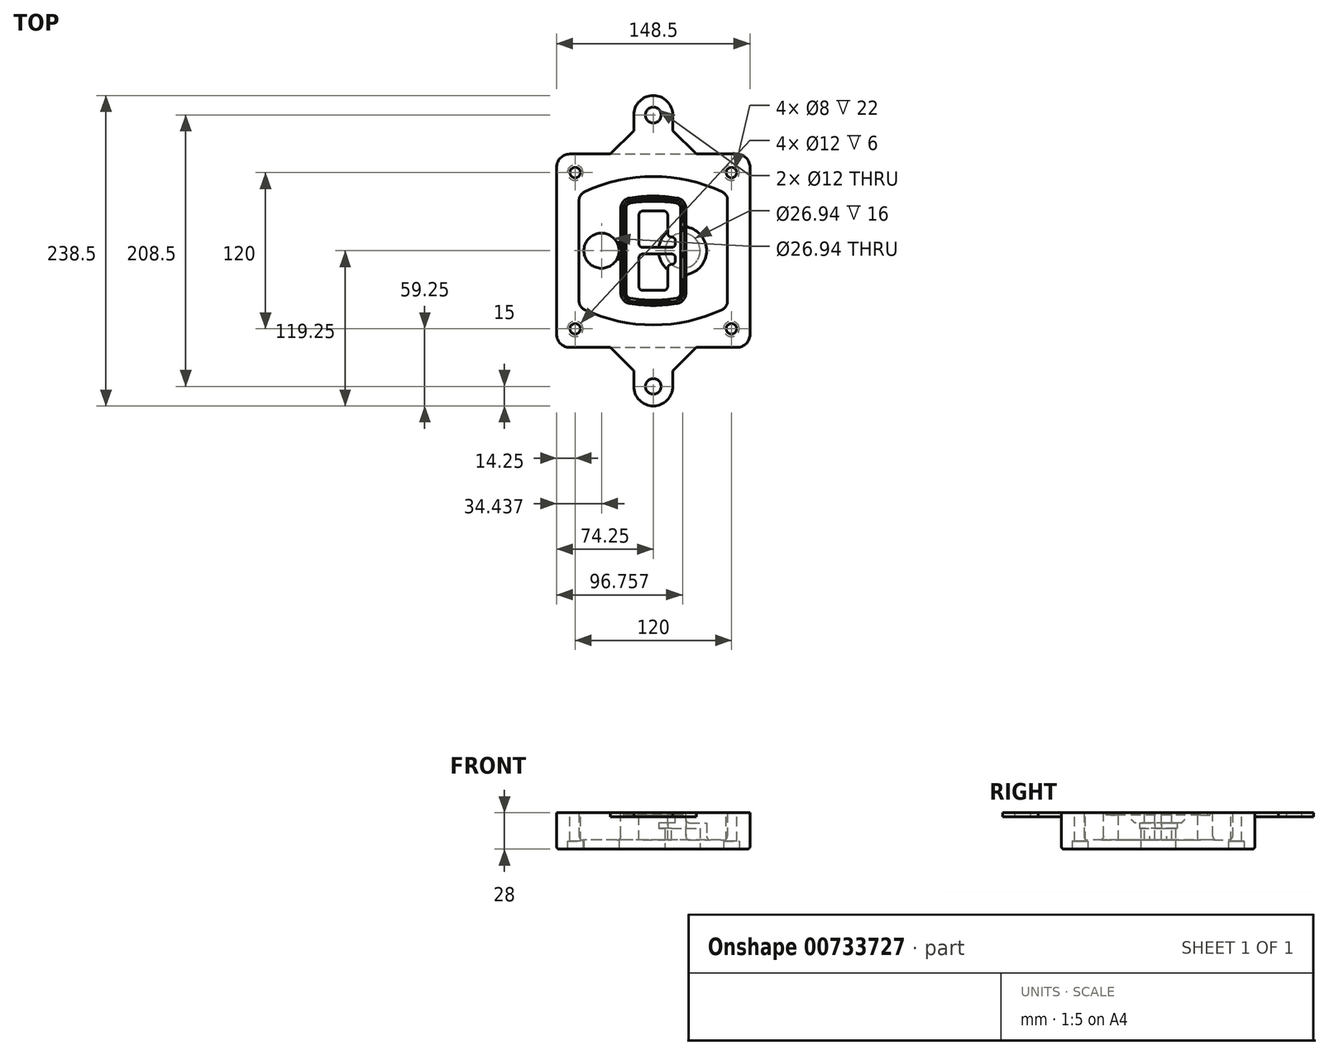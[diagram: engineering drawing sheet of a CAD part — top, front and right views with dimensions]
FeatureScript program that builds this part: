
annotation { "Feature Type Name" : "Feature", "Feature Type Description" : "" }
export const myFeature = defineFeature(function(context is Context, id is Id, definition is map)
    precondition{}
    {
        {
            var Q0;
            Q0=qCreatedBy(makeId("Top.planeOp"),FACE);
            var sketch = newSketch(context, id + "F0", { "sketchPlane" : qUnion([Q0])});
            skPoint(sketch, "E0.rect.middle", {"position": v(0, 0) * mm});
            skLineSegment(sketch, "E1.bottom", {"start": v(-64.25, -74.25) * mm, "end": v(64.25, -74.25) * mm});
            skLineSegment(sketch, "E1.top", {"start": v(-64.25, 74.25) * mm, "end": v(64.25, 74.25) * mm});
            skLineSegment(sketch, "E1.left", {"start": v(-74.25, -64.25) * mm, "end": v(-74.25, 64.25) * mm});
            skLineSegment(sketch, "E1.right", {"start": v(74.25, -64.25) * mm, "end": v(74.25, 64.25) * mm});
            skLineSegment(sketch, "E2", {"start": v(-74.25, 74.25) * mm, "end": v(74.25, -74.25) * mm, "construction": true});
            skLineSegment(sketch, "E3", {"start": v(74.25, 74.25) * mm, "end": v(-74.25, -74.25) * mm, "construction": true});
            skCircle(sketch, "E4", {"center": v(-60, 60) * mm, "radius": 4 * mm});
            skCircle(sketch, "E5", {"center": v(60, 60) * mm, "radius": 4 * mm});
            skCircle(sketch, "E6", {"center": v(60, -60) * mm, "radius": 4 * mm});
            skCircle(sketch, "E7", {"center": v(-60, -60) * mm, "radius": 4 * mm});
            skLineSegment(sketch, "E8", {"start": v(-60, 60) * mm, "end": v(60, 60) * mm, "construction": true});
            skLineSegment(sketch, "E9", {"start": v(60, 60) * mm, "end": v(60, -60) * mm, "construction": true});
            skLineSegment(sketch, "E10", {"start": v(60, -60) * mm, "end": v(-60, -60) * mm, "construction": true});
            skLineSegment(sketch, "E11", {"start": v(-60, -60) * mm, "end": v(-60, 60) * mm, "construction": true});
            skLineSegment(sketch, "E12", {"start": v(-60, 38.83) * mm, "end": v(-60, -38.83) * mm});
            skLineSegment(sketch, "E13", {"start": v(60, 38.83) * mm, "end": v(60, -38.83) * mm});
            skArc(sketch, "E14", {"start": v(54.26, 47.88) * mm, "mid": v(0, 60) * mm, "end": v(-54.26, 47.88) * mm});
            skArc(sketch, "E15", {"start": v(-54.26, -47.88) * mm, "mid": v(0, -60) * mm, "end": v(54.26, -47.88) * mm});
            skLineSegment(sketch, "E16", {"start": v(-60, 0) * mm, "end": v(60, 0) * mm, "construction": true});
            skPoint(sketch, "E17.visualSharp", {"position": v(-60, -45) * mm});
            skArc(sketch, "E17.filletArc", {"start": v(-60, -38.83) * mm, "mid": v(-58.44, -44.2) * mm, "end": v(-54.26, -47.88) * mm});
            skPoint(sketch, "E18.visualSharp", {"position": v(-60, 45) * mm});
            skArc(sketch, "E18.filletArc", {"start": v(-54.26, 47.88) * mm, "mid": v(-58.44, 44.2) * mm, "end": v(-60, 38.83) * mm});
            skPoint(sketch, "E19.visualSharp", {"position": v(60, 45) * mm});
            skArc(sketch, "E19.filletArc", {"start": v(60, 38.83) * mm, "mid": v(58.44, 44.2) * mm, "end": v(54.26, 47.88) * mm});
            skPoint(sketch, "E20.visualSharp", {"position": v(60, -45) * mm});
            skArc(sketch, "E20.filletArc", {"start": v(54.26, -47.88) * mm, "mid": v(58.44, -44.2) * mm, "end": v(60, -38.83) * mm});
            skPoint(sketch, "E21.visualSharp", {"position": v(-74.25, 74.25) * mm});
            skArc(sketch, "E21.filletArc", {"start": v(-64.25, 74.25) * mm, "mid": v(-71.32, 71.32) * mm, "end": v(-74.25, 64.25) * mm});
            skPoint(sketch, "E22.visualSharp", {"position": v(74.25, 74.25) * mm});
            skArc(sketch, "E22.filletArc", {"start": v(74.25, 64.25) * mm, "mid": v(71.32, 71.32) * mm, "end": v(64.25, 74.25) * mm});
            skPoint(sketch, "E23.visualSharp", {"position": v(74.25, -74.25) * mm});
            skArc(sketch, "E23.filletArc", {"start": v(64.25, -74.25) * mm, "mid": v(71.32, -71.32) * mm, "end": v(74.25, -64.25) * mm});
            skPoint(sketch, "E24.visualSharp", {"position": v(-74.25, -74.25) * mm});
            skArc(sketch, "E24.filletArc", {"start": v(-74.25, -64.25) * mm, "mid": v(-71.32, -71.32) * mm, "end": v(-64.25, -74.25) * mm});
            skArc(sketch, "E25.0", {"start": v(57, 38.83) * mm, "mid": v(55.9, 42.58) * mm, "end": v(52.98, 45.17) * mm});
            skLineSegment(sketch, "E25.1", {"start": v(57, 38.83) * mm, "end": v(57, -38.83) * mm});
            skArc(sketch, "E25.2", {"start": v(52.98, -45.17) * mm, "mid": v(55.9, -42.58) * mm, "end": v(57, -38.83) * mm});
            skArc(sketch, "E25.3", {"start": v(-52.98, -45.17) * mm, "mid": v(0, -57) * mm, "end": v(52.98, -45.17) * mm});
            skArc(sketch, "E25.4", {"start": v(-57, -38.83) * mm, "mid": v(-55.9, -42.58) * mm, "end": v(-52.98, -45.17) * mm});
            skArc(sketch, "E25.5", {"start": v(52.98, 45.17) * mm, "mid": v(0, 57) * mm, "end": v(-52.98, 45.17) * mm});
            skLineSegment(sketch, "E25.6", {"start": v(-57, 38.83) * mm, "end": v(-57, -38.83) * mm});
            skArc(sketch, "E25.7", {"start": v(-52.98, 45.17) * mm, "mid": v(-55.9, 42.58) * mm, "end": v(-57, 38.83) * mm});
            skArc(sketch, "E26.0", {"start": v(-55.96, 51.5) * mm, "mid": v(-61.82, 46.33) * mm, "end": v(-64, 38.83) * mm});
            skArc(sketch, "E26.1", {"start": v(55.96, 51.5) * mm, "mid": v(0, 64) * mm, "end": v(-55.96, 51.5) * mm});
            skArc(sketch, "E26.2", {"start": v(64, 38.83) * mm, "mid": v(61.82, 46.33) * mm, "end": v(55.96, 51.5) * mm});
            skLineSegment(sketch, "E26.3", {"start": v(64, 38.83) * mm, "end": v(64, -38.83) * mm});
            skArc(sketch, "E26.4", {"start": v(55.96, -51.5) * mm, "mid": v(61.82, -46.33) * mm, "end": v(64, -38.83) * mm});
            skLineSegment(sketch, "E26.5", {"start": v(-64, 38.83) * mm, "end": v(-64, -38.83) * mm});
            skArc(sketch, "E26.6", {"start": v(-55.96, -51.5) * mm, "mid": v(0, -64) * mm, "end": v(55.96, -51.5) * mm});
            skArc(sketch, "E26.7", {"start": v(-64, -38.83) * mm, "mid": v(-61.82, -46.33) * mm, "end": v(-55.96, -51.5) * mm});
            skSolve(sketch);
        }
        {
            var Q0;
            Q0=makeQuery(id+"F0.imprint","IMPRINT",FACE,{"disambiguationData":[TD([[makeQuery(id+"F0.imprint","IMPRINT",EDGE,{"derivedFrom":sQuery(id+"F0.wireOp",EDGE,"E1.bottom")}),1.0]])]});
            var Q1;
            Q1=makeQuery(id+"F0.imprint","IMPRINT",FACE,{"disambiguationData":[TD([[makeQuery(id+"F0.imprint","IMPRINT",EDGE,{"derivedFrom":sQuery(id+"F0.wireOp",EDGE,"E12")}),1.0]])]});
            var Q2;
            Q2=makeQuery(id+"F0.imprint","IMPRINT",FACE,{"disambiguationData":[TD([[makeQuery(id+"F0.imprint","IMPRINT",EDGE,{"derivedFrom":sQuery(id+"F0.wireOp",EDGE,"E25.0")}),1.0]])]});
            var Q3;
            Q3=makeQuery(id+"F0.imprint","IMPRINT",FACE,{"disambiguationData":[TD([[makeQuery(id+"F0.imprint","IMPRINT",EDGE,{"derivedFrom":sQuery(id+"F0.wireOp",EDGE,"E12")}),-1.0]])]});
            extrude(context, id + "F1", {"entities" : qUnion([Q0, Q1, Q2, Q3]), "oppositeDirection" : true, "depth" : 25 * mm});
        }
        {
            var Q0;
            Q0=makeQuery(id+"F0.imprint","IMPRINT",FACE,{"disambiguationData":[TD([[makeQuery(id+"F0.imprint","IMPRINT",EDGE,{"derivedFrom":sQuery(id+"F0.wireOp",EDGE,"E12")}),1.0]])]});
            extrude(context, id + "F2", {"entities" : qUnion([Q0]), "operationType" : NewBodyOperationType.ADD, "depth" : 3 * mm});
        }
        {
            var Q0;
            Q0=makeQuery(id+"F0.imprint","IMPRINT",FACE,{"disambiguationData":[TD([[makeQuery(id+"F0.imprint","IMPRINT",EDGE,{"derivedFrom":sQuery(id+"F0.wireOp",EDGE,"E25.0")}),1.0]])]});
            extrude(context, id + "F3", {"entities" : qUnion([Q0]), "operationType" : NewBodyOperationType.REMOVE, "oppositeDirection" : true, "depth" : 18 * mm});
        }
        {
            var Q0;
            Q0=makeQuery(id+"F2.opExtrude","CAP_FACE",FACE,{"disambiguationData":[OSD([sQuery(id+"F0.wireOp",EDGE,"E12"),sQuery(id+"F0.wireOp",EDGE,"E13"),sQuery(id+"F0.wireOp",EDGE,"E14"),sQuery(id+"F0.wireOp",EDGE,"E15"),sQuery(id+"F0.wireOp",EDGE,"E17.filletArc"),sQuery(id+"F0.wireOp",EDGE,"E18.filletArc"),sQuery(id+"F0.wireOp",EDGE,"E19.filletArc"),sQuery(id+"F0.wireOp",EDGE,"E20.filletArc"),sQuery(id+"F0.wireOp",EDGE,"E25.0"),sQuery(id+"F0.wireOp",EDGE,"E25.1"),sQuery(id+"F0.wireOp",EDGE,"E25.2"),sQuery(id+"F0.wireOp",EDGE,"E25.3"),sQuery(id+"F0.wireOp",EDGE,"E25.4"),sQuery(id+"F0.wireOp",EDGE,"E25.5"),sQuery(id+"F0.wireOp",EDGE,"E25.6"),sQuery(id+"F0.wireOp",EDGE,"E25.7")])],"isStart":false});
            var sketch = newSketch(context, id + "F4", { "sketchPlane" : qUnion([Q0])});
            skArc(sketch, "E27.0", {"start": v(-18.34, -40.45) * mm, "mid": v(0, -42) * mm, "end": v(18.34, -40.45) * mm});
            skArc(sketch, "E28.0", {"start": v(18.34, 40.45) * mm, "mid": v(0, 42) * mm, "end": v(-18.34, 40.45) * mm});
            skLineSegment(sketch, "E29", {"start": v(-25, 32.57) * mm, "end": v(-25, -32.57) * mm});
            skLineSegment(sketch, "E30", {"start": v(25, 32.57) * mm, "end": v(25, -32.57) * mm});
            skLineSegment(sketch, "E31", {"start": v(-25, 39.1) * mm, "end": v(25, 39.1) * mm, "construction": true});
            skLineSegment(sketch, "E32", {"start": v(-25, -39.1) * mm, "end": v(25, -39.1) * mm, "construction": true});
            skPoint(sketch, "E33.visualSharp", {"position": v(-25, 39.1) * mm});
            skArc(sketch, "E33.filletArc", {"start": v(-18.34, 40.45) * mm, "mid": v(-23.11, 37.73) * mm, "end": v(-25, 32.57) * mm});
            skPoint(sketch, "E34.visualSharp", {"position": v(25, 39.1) * mm});
            skArc(sketch, "E34.filletArc", {"start": v(25, 32.57) * mm, "mid": v(23.11, 37.73) * mm, "end": v(18.34, 40.45) * mm});
            skPoint(sketch, "E35.visualSharp", {"position": v(25, -39.1) * mm});
            skArc(sketch, "E35.filletArc", {"start": v(18.34, -40.45) * mm, "mid": v(23.11, -37.73) * mm, "end": v(25, -32.57) * mm});
            skPoint(sketch, "E36.visualSharp", {"position": v(-25, -39.1) * mm});
            skArc(sketch, "E36.filletArc", {"start": v(-25, -32.57) * mm, "mid": v(-23.11, -37.73) * mm, "end": v(-18.34, -40.45) * mm});
            skArc(sketch, "E37.0", {"start": v(52.98, 45.17) * mm, "mid": v(0, 57) * mm, "end": v(-52.98, 45.17) * mm});
            skArc(sketch, "E37.1", {"start": v(-52.98, 45.17) * mm, "mid": v(-55.9, 42.58) * mm, "end": v(-57, 38.83) * mm});
            skLineSegment(sketch, "E37.2", {"start": v(-57, 38.83) * mm, "end": v(-57, -38.83) * mm});
            skArc(sketch, "E37.3", {"start": v(-57, -38.83) * mm, "mid": v(-55.9, -42.58) * mm, "end": v(-52.98, -45.17) * mm});
            skArc(sketch, "E37.4", {"start": v(-52.98, -45.17) * mm, "mid": v(0, -57) * mm, "end": v(52.98, -45.17) * mm});
            skArc(sketch, "E37.5", {"start": v(52.98, -45.17) * mm, "mid": v(55.9, -42.58) * mm, "end": v(57, -38.83) * mm});
            skLineSegment(sketch, "E37.6", {"start": v(57, 38.83) * mm, "end": v(57, -38.83) * mm});
            skArc(sketch, "E37.7", {"start": v(57, 38.83) * mm, "mid": v(55.9, 42.58) * mm, "end": v(52.98, 45.17) * mm});
            skLineSegment(sketch, "E38.0", {"start": v(23, 32.57) * mm, "end": v(23, -32.57) * mm});
            skArc(sketch, "E38.1", {"start": v(18, -38.48) * mm, "mid": v(21.58, -36.44) * mm, "end": v(23, -32.57) * mm});
            skArc(sketch, "E38.2", {"start": v(-18, -38.48) * mm, "mid": v(0, -40) * mm, "end": v(18, -38.48) * mm});
            skArc(sketch, "E38.3", {"start": v(-23, -32.57) * mm, "mid": v(-21.58, -36.44) * mm, "end": v(-18, -38.48) * mm});
            skLineSegment(sketch, "E38.4", {"start": v(-23, 32.57) * mm, "end": v(-23, -32.57) * mm});
            skArc(sketch, "E38.5", {"start": v(23, 32.57) * mm, "mid": v(21.58, 36.44) * mm, "end": v(18, 38.48) * mm});
            skArc(sketch, "E38.6", {"start": v(-18, 38.48) * mm, "mid": v(-21.58, 36.44) * mm, "end": v(-23, 32.57) * mm});
            skArc(sketch, "E38.7", {"start": v(18, 38.48) * mm, "mid": v(0, 40) * mm, "end": v(-18, 38.48) * mm});
            skArc(sketch, "E39.0", {"start": v(21, 32.57) * mm, "mid": v(20.06, 35.15) * mm, "end": v(17.67, 36.5) * mm});
            skLineSegment(sketch, "E39.1", {"start": v(21, 32.57) * mm, "end": v(21, -32.57) * mm});
            skArc(sketch, "E39.2", {"start": v(17.67, -36.5) * mm, "mid": v(20.06, -35.15) * mm, "end": v(21, -32.57) * mm});
            skArc(sketch, "E39.3", {"start": v(-17.67, -36.5) * mm, "mid": v(0, -38) * mm, "end": v(17.67, -36.5) * mm});
            skArc(sketch, "E39.4", {"start": v(-21, -32.57) * mm, "mid": v(-20.06, -35.15) * mm, "end": v(-17.67, -36.5) * mm});
            skArc(sketch, "E39.5", {"start": v(17.67, 36.5) * mm, "mid": v(0, 38) * mm, "end": v(-17.67, 36.5) * mm});
            skLineSegment(sketch, "E39.6", {"start": v(-21, 32.57) * mm, "end": v(-21, -32.57) * mm});
            skArc(sketch, "E39.7", {"start": v(-17.67, 36.5) * mm, "mid": v(-20.06, 35.15) * mm, "end": v(-21, 32.57) * mm});
            skLineSegment(sketch, "E40", {"start": v(-25, 0) * mm, "end": v(25, 0) * mm, "construction": true});
            skLineSegment(sketch, "E41", {"start": v(-11, 5.5) * mm, "end": v(-11, 27.5) * mm});
            skLineSegment(sketch, "E42", {"start": v(-8, 30.5) * mm, "end": v(8, 30.5) * mm});
            skLineSegment(sketch, "E43", {"start": v(11, 27.5) * mm, "end": v(11, 13.5) * mm});
            skLineSegment(sketch, "E44", {"start": v(14, 10.5) * mm, "end": v(14, 10.5) * mm});
            skLineSegment(sketch, "E45", {"start": v(17, 7.5) * mm, "end": v(17, 5.5) * mm});
            skLineSegment(sketch, "E46", {"start": v(14, 2.5) * mm, "end": v(-8, 2.5) * mm});
            skPoint(sketch, "E47.visualSharp", {"position": v(-11, 30.5) * mm});
            skArc(sketch, "E47.filletArc", {"start": v(-8, 30.5) * mm, "mid": v(-10.12, 29.62) * mm, "end": v(-11, 27.5) * mm});
            skPoint(sketch, "E48.visualSharp", {"position": v(11, 30.5) * mm});
            skArc(sketch, "E48.filletArc", {"start": v(11, 27.5) * mm, "mid": v(10.12, 29.62) * mm, "end": v(8, 30.5) * mm});
            skPoint(sketch, "E49.visualSharp", {"position": v(11, 10.5) * mm});
            skArc(sketch, "E49.filletArc", {"start": v(11, 13.5) * mm, "mid": v(11.88, 11.38) * mm, "end": v(14, 10.5) * mm});
            skPoint(sketch, "E50.visualSharp", {"position": v(17, 10.5) * mm});
            skArc(sketch, "E50.filletArc", {"start": v(17, 7.5) * mm, "mid": v(16.12, 9.62) * mm, "end": v(14, 10.5) * mm});
            skPoint(sketch, "E51.visualSharp", {"position": v(17, 2.5) * mm});
            skArc(sketch, "E51.filletArc", {"start": v(14, 2.5) * mm, "mid": v(16.12, 3.38) * mm, "end": v(17, 5.5) * mm});
            skPoint(sketch, "E52.visualSharp", {"position": v(-11, 2.5) * mm});
            skArc(sketch, "E52.filletArc", {"start": v(-11, 5.5) * mm, "mid": v(-10.12, 3.38) * mm, "end": v(-8, 2.5) * mm});
            skLineSegment(sketch, "E53.0.MirrorCS", {"start": v(14, -2.5) * mm, "end": v(-8, -2.5) * mm});
            skArc(sketch, "E54.0.MirrorCS", {"start": v(-11, -5.5) * mm, "mid": v(-10.12, -3.38) * mm, "end": v(-8, -2.5) * mm});
            skLineSegment(sketch, "E55.0.MirrorCS", {"start": v(-11, -5.5) * mm, "end": v(-11, -27.5) * mm});
            skArc(sketch, "E56.0.MirrorCS", {"start": v(-8, -30.5) * mm, "mid": v(-10.12, -29.62) * mm, "end": v(-11, -27.5) * mm});
            skLineSegment(sketch, "E57.0.MirrorCS", {"start": v(-8, -30.5) * mm, "end": v(8, -30.5) * mm});
            skArc(sketch, "E58.0.MirrorCS", {"start": v(11, -27.5) * mm, "mid": v(10.12, -29.62) * mm, "end": v(8, -30.5) * mm});
            skLineSegment(sketch, "E59.0.MirrorCS", {"start": v(11, -27.5) * mm, "end": v(11, -13.5) * mm});
            skArc(sketch, "E60.0.MirrorCS", {"start": v(11, -13.5) * mm, "mid": v(11.88, -11.38) * mm, "end": v(14, -10.5) * mm});
            skArc(sketch, "E61.0.MirrorCS", {"start": v(17, -7.5) * mm, "mid": v(16.12, -9.62) * mm, "end": v(14, -10.5) * mm});
            skLineSegment(sketch, "E62.0.MirrorCS", {"start": v(17, -7.5) * mm, "end": v(17, -5.5) * mm});
            skArc(sketch, "E63.0.MirrorCS", {"start": v(14, -2.5) * mm, "mid": v(16.12, -3.38) * mm, "end": v(17, -5.5) * mm});
            skSolve(sketch);
        }
        {
            var Q0;
            Q0=makeQuery(id+"F4.imprint","IMPRINT",FACE,{"disambiguationData":[TD([[makeQuery(id+"F4.imprint","IMPRINT",EDGE,{"derivedFrom":sQuery(id+"F4.wireOp",EDGE,"E27.0")}),1.0]])]});
            var Q1;
            Q1=makeQuery(id+"F4.imprint","IMPRINT",FACE,{"disambiguationData":[TD([[makeQuery(id+"F4.imprint","IMPRINT",EDGE,{"derivedFrom":sQuery(id+"F4.wireOp",EDGE,"E38.0")}),-1.0]])]});
            var Q2;
            Q2=makeQuery(id+"F4.imprint","IMPRINT",FACE,{"disambiguationData":[TD([[makeQuery(id+"F4.imprint","IMPRINT",EDGE,{"derivedFrom":sQuery(id+"F4.wireOp",EDGE,"E39.0")}),1.0]])]});
            extrude(context, id + "F5", {"entities" : qUnion([Q0, Q1, Q2]), "operationType" : NewBodyOperationType.ADD, "endBound" : BoundingType.UP_TO_NEXT, "oppositeDirection" : true, "depth" : 25 * mm});
        }
        {
            var Q0;
            Q0=makeQuery(id+"F4.imprint","IMPRINT",FACE,{"disambiguationData":[TD([[makeQuery(id+"F4.imprint","IMPRINT",EDGE,{"derivedFrom":sQuery(id+"F4.wireOp",EDGE,"E38.0")}),-1.0]])]});
            extrude(context, id + "F6", {"entities" : qUnion([Q0]), "operationType" : NewBodyOperationType.REMOVE, "oppositeDirection" : true, "depth" : 2 * mm});
        }
        {
            var Q0;
            Q0=makeQuery(id+"F1.opExtrude","CAP_FACE",FACE,{"disambiguationData":[OSD([sQuery(id+"F0.wireOp",EDGE,"E1.bottom"),sQuery(id+"F0.wireOp",EDGE,"E1.top"),sQuery(id+"F0.wireOp",EDGE,"E1.left"),sQuery(id+"F0.wireOp",EDGE,"E1.right"),sQuery(id+"F0.wireOp",EDGE,"E4"),sQuery(id+"F0.wireOp",EDGE,"E5"),sQuery(id+"F0.wireOp",EDGE,"E6"),sQuery(id+"F0.wireOp",EDGE,"E7"),sQuery(id+"F0.wireOp",EDGE,"E21.filletArc"),sQuery(id+"F0.wireOp",EDGE,"E22.filletArc"),sQuery(id+"F0.wireOp",EDGE,"E23.filletArc"),sQuery(id+"F0.wireOp",EDGE,"E24.filletArc")])],"isStart":false});
            var sketch = newSketch(context, id + "F7", { "sketchPlane" : qUnion([Q0])});
            skCircle(sketch, "E64", {"center": v(22.5, 0) * mm, "radius": 13.47 * mm});
            skCircle(sketch, "E65", {"center": v(-39.81, 0) * mm, "radius": 13.47 * mm});
            skLineSegment(sketch, "E66", {"start": v(74.25, 0) * mm, "end": v(-74.25, 0) * mm});
            skCircle(sketch, "E67", {"center": v(22.5, 0) * mm, "radius": 18.47 * mm});
            skCircle(sketch, "E68", {"center": v(60, -60) * mm, "radius": 6 * mm});
            skCircle(sketch, "E69", {"center": v(-60, -60) * mm, "radius": 6 * mm});
            skCircle(sketch, "E70", {"center": v(-60, 60) * mm, "radius": 6 * mm});
            skCircle(sketch, "E71", {"center": v(60, 60) * mm, "radius": 6 * mm});
            skSolve(sketch);
        }
        {
            var Q0;
            {var subQ1=sQuery(id+"F7.wireOp",EDGE,"E66");var subQ4=sQuery(id+"F7.wireOp",EDGE,"E64");var subQ6=makeQuery(id+"F7.imprint","INTERSECT",VERTEX,{"disambiguationData":[OD(0.0)],"derivedFrom":[subQ4,subQ1]});Q0=makeQuery(id+"F7.imprint","IMPRINT",FACE,{"disambiguationData":[TD([[makeQuery(id+"F7.imprint","IMPRINT",EDGE,{"disambiguationData":[TD([[subQ6,-1.0]])],"derivedFrom":subQ4}),-1.0]])]});}
            var Q1;
            {var subQ0=sQuery(id+"F7.wireOp",EDGE,"E66");var subQ1=sQuery(id+"F7.wireOp",EDGE,"E64");var subQ3=makeQuery(id+"F7.imprint","INTERSECT",VERTEX,{"disambiguationData":[OD(0.0)],"derivedFrom":[subQ1,subQ0]});Q1=makeQuery(id+"F7.imprint","IMPRINT",FACE,{"disambiguationData":[TD([[makeQuery(id+"F7.imprint","IMPRINT",EDGE,{"disambiguationData":[TD([[subQ3,-1.0]])],"derivedFrom":subQ1}),1.0]])]});}
            var Q2;
            {var subQ0=sQuery(id+"F7.wireOp",EDGE,"E66");var subQ1=sQuery(id+"F7.wireOp",EDGE,"E64");var subQ3=makeQuery(id+"F7.imprint","INTERSECT",VERTEX,{"disambiguationData":[OD(0.0)],"derivedFrom":[subQ1,subQ0]});Q2=makeQuery(id+"F7.imprint","IMPRINT",FACE,{"disambiguationData":[TD([[makeQuery(id+"F7.imprint","IMPRINT",EDGE,{"disambiguationData":[TD([[subQ3,1.0]])],"derivedFrom":subQ1}),1.0]])]});}
            var Q3;
            {var subQ1=sQuery(id+"F7.wireOp",EDGE,"E66");var subQ4=sQuery(id+"F7.wireOp",EDGE,"E64");var subQ6=makeQuery(id+"F7.imprint","INTERSECT",VERTEX,{"disambiguationData":[OD(0.0)],"derivedFrom":[subQ4,subQ1]});Q3=makeQuery(id+"F7.imprint","IMPRINT",FACE,{"disambiguationData":[TD([[makeQuery(id+"F7.imprint","IMPRINT",EDGE,{"disambiguationData":[TD([[subQ6,1.0]])],"derivedFrom":subQ4}),-1.0]])]});}
            extrude(context, id + "F8", {"entities" : qUnion([Q0, Q1, Q2, Q3]), "operationType" : NewBodyOperationType.ADD, "oppositeDirection" : true, "depth" : 20 * mm});
        }
        {
            var Q0;
            {var subQ0=sQuery(id+"F7.wireOp",EDGE,"E66");var subQ1=sQuery(id+"F7.wireOp",EDGE,"E64");var subQ3=makeQuery(id+"F7.imprint","INTERSECT",VERTEX,{"disambiguationData":[OD(0.0)],"derivedFrom":[subQ1,subQ0]});Q0=makeQuery(id+"F7.imprint","IMPRINT",FACE,{"disambiguationData":[TD([[makeQuery(id+"F7.imprint","IMPRINT",EDGE,{"disambiguationData":[TD([[subQ3,-1.0]])],"derivedFrom":subQ1}),1.0]])]});}
            var Q1;
            {var subQ0=sQuery(id+"F7.wireOp",EDGE,"E66");var subQ1=sQuery(id+"F7.wireOp",EDGE,"E64");var subQ3=makeQuery(id+"F7.imprint","INTERSECT",VERTEX,{"disambiguationData":[OD(0.0)],"derivedFrom":[subQ1,subQ0]});Q1=makeQuery(id+"F7.imprint","IMPRINT",FACE,{"disambiguationData":[TD([[makeQuery(id+"F7.imprint","IMPRINT",EDGE,{"disambiguationData":[TD([[subQ3,1.0]])],"derivedFrom":subQ1}),1.0]])]});}
            extrude(context, id + "F9", {"entities" : qUnion([Q0, Q1]), "operationType" : NewBodyOperationType.REMOVE, "oppositeDirection" : true, "depth" : 16 * mm});
        }
        {
            var Q0;
            {var subQ0=sQuery(id+"F7.wireOp",EDGE,"E66");var subQ1=sQuery(id+"F7.wireOp",EDGE,"E65");var subQ3=makeQuery(id+"F7.imprint","INTERSECT",VERTEX,{"disambiguationData":[OD(0.0)],"derivedFrom":[subQ1,subQ0]});Q0=makeQuery(id+"F7.imprint","IMPRINT",FACE,{"disambiguationData":[TD([[makeQuery(id+"F7.imprint","IMPRINT",EDGE,{"disambiguationData":[TD([[subQ3,-1.0]])],"derivedFrom":subQ1}),1.0]])]});}
            var Q1;
            {var subQ0=sQuery(id+"F7.wireOp",EDGE,"E66");var subQ1=sQuery(id+"F7.wireOp",EDGE,"E65");var subQ3=makeQuery(id+"F7.imprint","INTERSECT",VERTEX,{"disambiguationData":[OD(0.0)],"derivedFrom":[subQ1,subQ0]});Q1=makeQuery(id+"F7.imprint","IMPRINT",FACE,{"disambiguationData":[TD([[makeQuery(id+"F7.imprint","IMPRINT",EDGE,{"disambiguationData":[TD([[subQ3,1.0]])],"derivedFrom":subQ1}),1.0]])]});}
            extrude(context, id + "F10", {"entities" : qUnion([Q0, Q1]), "operationType" : NewBodyOperationType.REMOVE, "oppositeDirection" : true, "depth" : 25 * mm});
        }
        {
            var Q0;
            Q0=makeQuery(id+"F7.imprint","IMPRINT",FACE,{"disambiguationData":[TD([[makeQuery(id+"F7.imprint","IMPRINT",EDGE,{"derivedFrom":sQuery(id+"F7.wireOp",EDGE,"E68")}),1.0]])]});
            var Q1;
            Q1=makeQuery(id+"F7.imprint","IMPRINT",FACE,{"disambiguationData":[TD([[makeQuery(id+"F7.imprint","IMPRINT",EDGE,{"derivedFrom":makeQuery(id+"F1.opExtrude","CAP_EDGE",EDGE,{"disambiguationData":[OSD([sQuery(id+"F0.wireOp",EDGE,"E5")])],"isStart":false})}),-1.0]])]});
            var Q2;
            Q2=makeQuery(id+"F7.imprint","IMPRINT",FACE,{"disambiguationData":[TD([[makeQuery(id+"F7.imprint","IMPRINT",EDGE,{"derivedFrom":sQuery(id+"F7.wireOp",EDGE,"E69")}),1.0]])]});
            var Q3;
            Q3=makeQuery(id+"F7.imprint","IMPRINT",FACE,{"disambiguationData":[TD([[makeQuery(id+"F7.imprint","IMPRINT",EDGE,{"derivedFrom":makeQuery(id+"F1.opExtrude","CAP_EDGE",EDGE,{"disambiguationData":[OSD([sQuery(id+"F0.wireOp",EDGE,"E4")])],"isStart":false})}),-1.0]])]});
            var Q4;
            Q4=makeQuery(id+"F7.imprint","IMPRINT",FACE,{"disambiguationData":[TD([[makeQuery(id+"F7.imprint","IMPRINT",EDGE,{"derivedFrom":sQuery(id+"F7.wireOp",EDGE,"E70")}),1.0]])]});
            var Q5;
            Q5=makeQuery(id+"F7.imprint","IMPRINT",FACE,{"disambiguationData":[TD([[makeQuery(id+"F7.imprint","IMPRINT",EDGE,{"derivedFrom":makeQuery(id+"F1.opExtrude","CAP_EDGE",EDGE,{"disambiguationData":[OSD([sQuery(id+"F0.wireOp",EDGE,"E7")])],"isStart":false})}),-1.0]])]});
            var Q6;
            Q6=makeQuery(id+"F7.imprint","IMPRINT",FACE,{"disambiguationData":[TD([[makeQuery(id+"F7.imprint","IMPRINT",EDGE,{"derivedFrom":sQuery(id+"F7.wireOp",EDGE,"E71")}),1.0]])]});
            var Q7;
            Q7=makeQuery(id+"F7.imprint","IMPRINT",FACE,{"disambiguationData":[TD([[makeQuery(id+"F7.imprint","IMPRINT",EDGE,{"derivedFrom":makeQuery(id+"F1.opExtrude","CAP_EDGE",EDGE,{"disambiguationData":[OSD([sQuery(id+"F0.wireOp",EDGE,"E6")])],"isStart":false})}),-1.0]])]});
            extrude(context, id + "F11", {"entities" : qUnion([Q0, Q1, Q2, Q3, Q4, Q5, Q6, Q7]), "operationType" : NewBodyOperationType.REMOVE, "oppositeDirection" : true, "depth" : 6 * mm});
        }
        {
            var Q0;
            Q0=makeQuery(id+"F9.boolean.opBoolean","COPY",FACE,{"derivedFrom":makeQuery(id+"F9.opExtrude","CAP_FACE",FACE,{"disambiguationData":[OSD([sQuery(id+"F7.wireOp",EDGE,"E64")])],"isStart":false})});
            var sketch = newSketch(context, id + "F12", { "sketchPlane" : qUnion([Q0])});
            skArc(sketch, "E72.0", {"start": v(11, 14.45) * mm, "mid": v(6.45, 9.13) * mm, "end": v(4.2, 2.5) * mm});
            skArc(sketch, "E72.1", {"start": v(4.2, -2.5) * mm, "mid": v(6.45, -9.13) * mm, "end": v(11, -14.45) * mm});
            skLineSegment(sketch, "E73", {"start": v(4.2, -2.5) * mm, "end": v(14, -2.5) * mm});
            skLineSegment(sketch, "E74.0", {"start": v(14, 2.5) * mm, "end": v(4.2, 2.5) * mm});
            skArc(sketch, "E74.1", {"start": v(14, 2.5) * mm, "mid": v(16.12, 3.38) * mm, "end": v(17, 5.5) * mm});
            skLineSegment(sketch, "E74.2", {"start": v(17, 7.5) * mm, "end": v(17, 5.5) * mm});
            skArc(sketch, "E74.3", {"start": v(17, 7.5) * mm, "mid": v(16.12, 9.62) * mm, "end": v(14, 10.5) * mm});
            skArc(sketch, "E74.4", {"start": v(11, 13.5) * mm, "mid": v(11.88, 11.38) * mm, "end": v(14, 10.5) * mm});
            skLineSegment(sketch, "E74.5", {"start": v(11, 14.45) * mm, "end": v(11, 13.5) * mm});
            skLineSegment(sketch, "E74.7", {"start": v(14, -2.5) * mm, "end": v(4.2, -2.5) * mm});
            skArc(sketch, "E74.8", {"start": v(14, -2.5) * mm, "mid": v(16.12, -3.38) * mm, "end": v(17, -5.5) * mm});
            skLineSegment(sketch, "E74.9", {"start": v(17, -7.5) * mm, "end": v(17, -5.5) * mm});
            skArc(sketch, "E74.10", {"start": v(17, -7.5) * mm, "mid": v(16.12, -9.62) * mm, "end": v(14, -10.5) * mm});
            skArc(sketch, "E74.11", {"start": v(11, -13.5) * mm, "mid": v(11.88, -11.38) * mm, "end": v(14, -10.5) * mm});
            skLineSegment(sketch, "E74.12", {"start": v(11, -14.45) * mm, "end": v(11, -13.5) * mm});
            skPoint(sketch, "E75.orphan", {"position": v(11, -27.5) * mm});
            skPoint(sketch, "E76.orphan", {"position": v(-8, -2.5) * mm});
            skPoint(sketch, "E77.orphan", {"position": v(-8, 2.5) * mm});
            skPoint(sketch, "E78.orphan", {"position": v(11, 27.5) * mm});
            skSolve(sketch);
        }
        {
            var Q0;
            {var subQ7=sQuery(id+"F12.wireOp",EDGE,"E72.0");var subQ14=sQuery(id+"F12.wireOp",EDGE,"E72.1");var subQ16=sQuery(id+"F12.wireOp",EDGE,"E74.1");var subQ18=sQuery(id+"F12.wireOp",EDGE,"E74.8");Q0=qUnion([makeQuery(id+"F12.imprint","IMPRINT",FACE,{"disambiguationData":[TD([[makeQuery(id+"F12.imprint","IMPRINT",EDGE,{"derivedFrom":subQ7}),1.0]])]}),makeQuery(id+"F12.imprint","IMPRINT",FACE,{"disambiguationData":[TD([[makeQuery(id+"F12.imprint","IMPRINT",EDGE,{"derivedFrom":subQ14}),1.0]])]}),makeQuery(id+"F12.imprint","IMPRINT",FACE,{"disambiguationData":[TD([[makeQuery(id+"F12.imprint","IMPRINT",EDGE,{"derivedFrom":subQ16}),1.0]])]}),makeQuery(id+"F12.imprint","IMPRINT",FACE,{"disambiguationData":[TD([[makeQuery(id+"F12.imprint","IMPRINT",EDGE,{"derivedFrom":subQ18}),-1.0]])]})]);}
            var Q1;
            Q1=makeQuery(id+"F5.boolean.opBoolean","SPLIT",FACE,{"disambiguationData":[TD([makeQuery(id+"F5.opExtrude","SWEPT_FACE",FACE,{"disambiguationData":[OSD([sQuery(id+"F4.wireOp",EDGE,"E41")])]})])],"derivedFrom":makeQuery(id+"F3.boolean.opBoolean","COPY",FACE,{"derivedFrom":makeQuery(id+"F3.opExtrude","CAP_FACE",FACE,{"disambiguationData":[OSD([sQuery(id+"F0.wireOp",EDGE,"E25.0"),sQuery(id+"F0.wireOp",EDGE,"E25.1"),sQuery(id+"F0.wireOp",EDGE,"E25.2"),sQuery(id+"F0.wireOp",EDGE,"E25.3"),sQuery(id+"F0.wireOp",EDGE,"E25.4"),sQuery(id+"F0.wireOp",EDGE,"E25.5"),sQuery(id+"F0.wireOp",EDGE,"E25.6"),sQuery(id+"F0.wireOp",EDGE,"E25.7")])],"isStart":false})})});
            extrude(context, id + "F13", {"entities" : qUnion([Q0]), "operationType" : NewBodyOperationType.REMOVE, "endBound" : BoundingType.UP_TO_SURFACE, "endBoundEntityFace" : qUnion([Q1]), "depth" : 25 * mm});
        }
        {
            var Q0;
            Q0=makeQuery(id+"F3.boolean.opBoolean","COPY",EDGE,{"derivedFrom":makeQuery(id+"F3.opExtrude","CAP_EDGE",EDGE,{"disambiguationData":[OSD([sQuery(id+"F0.wireOp",EDGE,"E25.6")])],"isStart":false})});
            var Q1;
            Q1=makeQuery(id+"F8.boolean.opBoolean","INTERSECT",EDGE,{"derivedFrom":[makeQuery(id+"F5.opExtrude","SWEPT_FACE",FACE,{"disambiguationData":[OSD([sQuery(id+"F4.wireOp",EDGE,"E30")])]}),makeQuery(id+"F8.opExtrude","CAP_FACE",FACE,{"disambiguationData":[OSD([sQuery(id+"F7.wireOp",EDGE,"E67")])],"isStart":false})]});
            var Q2;
            Q2=makeQuery(id+"F8.boolean.opBoolean","INTERSECT",EDGE,{"disambiguationData":[OD(1.0)],"derivedFrom":[makeQuery(id+"F5.opExtrude","SWEPT_FACE",FACE,{"disambiguationData":[OSD([sQuery(id+"F4.wireOp",EDGE,"E30")])]}),makeQuery(id+"F8.opExtrude","SWEPT_FACE",FACE,{"disambiguationData":[OSD([sQuery(id+"F7.wireOp",EDGE,"E67")])]})]});
            var Q3;
            {var subQ0=sQuery(id+"F4.wireOp",EDGE,"E30");Q3=makeQuery(id+"F8.boolean.opBoolean","SPLIT",EDGE,{"disambiguationData":[TD([makeQuery(id+"F5.opExtrude","SWEPT_FACE",FACE,{"disambiguationData":[OSD([sQuery(id+"F4.wireOp",EDGE,"E35.filletArc")])]})])],"derivedFrom":makeQuery(id+"F5.opExtrude","CAP_EDGE",EDGE,{"disambiguationData":[OSD([subQ0])],"isStart":false})});}
            var Q4;
            {var subQ0=sQuery(id+"F0.wireOp",EDGE,"E25.7");var subQ1=sQuery(id+"F0.wireOp",EDGE,"E25.1");var subQ2=sQuery(id+"F0.wireOp",EDGE,"E25.6");var subQ3=sQuery(id+"F0.wireOp",EDGE,"E25.5");var subQ4=sQuery(id+"F0.wireOp",EDGE,"E25.4");var subQ5=sQuery(id+"F0.wireOp",EDGE,"E25.0");var subQ6=sQuery(id+"F0.wireOp",EDGE,"E25.2");var subQ7=sQuery(id+"F0.wireOp",EDGE,"E25.3");Q4=makeQuery(id+"F8.boolean.opBoolean","INTERSECT",EDGE,{"derivedFrom":[makeQuery(id+"F5.boolean.opBoolean","SPLIT",FACE,{"disambiguationData":[TD([makeQuery(id+"F2.opExtrude","SWEPT_FACE",FACE,{"disambiguationData":[OSD([subQ5])]})])],"derivedFrom":makeQuery(id+"F3.boolean.opBoolean","COPY",FACE,{"derivedFrom":makeQuery(id+"F3.opExtrude","CAP_FACE",FACE,{"disambiguationData":[OSD([subQ5,subQ1,subQ6,subQ7,subQ4,subQ3,subQ2,subQ0])],"isStart":false})})}),makeQuery(id+"F8.opExtrude","SWEPT_FACE",FACE,{"disambiguationData":[OSD([sQuery(id+"F7.wireOp",EDGE,"E67")])]})]});}
            var Q5;
            Q5=makeQuery(id+"F8.boolean.opBoolean","INTERSECT",EDGE,{"disambiguationData":[OD(0.0)],"derivedFrom":[makeQuery(id+"F5.opExtrude","SWEPT_FACE",FACE,{"disambiguationData":[OSD([sQuery(id+"F4.wireOp",EDGE,"E30")])]}),makeQuery(id+"F8.opExtrude","SWEPT_FACE",FACE,{"disambiguationData":[OSD([sQuery(id+"F7.wireOp",EDGE,"E67")])]})]});
            fillet(context, id + "F14", {"entities" : qUnion([Q0, Q1, Q2, Q3, Q4, Q5]), "radius" : 3 * mm, "tangentPropagation" : true, "allowEdgeOverflow" : false});
        }
        {
            var Q0;
            Q0=makeQuery(id+"F1.opExtrude","CAP_EDGE",EDGE,{"disambiguationData":[OSD([sQuery(id+"F0.wireOp",EDGE,"E1.bottom")])],"isStart":false});
            fillet(context, id + "F15", {"entities" : qUnion([Q0]), "radius" : 2 * mm, "tangentPropagation" : true, "allowEdgeOverflow" : false});
        }
        {
            var Q0;
            {var subQ0=sQuery(id+"F0.wireOp",EDGE,"E21.filletArc");var subQ1=sQuery(id+"F0.wireOp",EDGE,"E7");var subQ2=sQuery(id+"F0.wireOp",EDGE,"E6");var subQ3=sQuery(id+"F0.wireOp",EDGE,"E5");var subQ4=sQuery(id+"F0.wireOp",EDGE,"E4");var subQ5=sQuery(id+"F0.wireOp",EDGE,"E22.filletArc");var subQ6=sQuery(id+"F0.wireOp",EDGE,"E1.bottom");var subQ7=sQuery(id+"F0.wireOp",EDGE,"E1.right");var subQ8=sQuery(id+"F0.wireOp",EDGE,"E1.top");var subQ9=sQuery(id+"F0.wireOp",EDGE,"E1.left");var subQ10=sQuery(id+"F0.wireOp",EDGE,"E23.filletArc");var subQ11=sQuery(id+"F0.wireOp",EDGE,"E24.filletArc");Q0=makeQuery(id+"F2.boolean.opBoolean","SPLIT",FACE,{"disambiguationData":[TD([makeQuery(id+"F1.opExtrude","SWEPT_FACE",FACE,{"disambiguationData":[OSD([subQ6])]})])],"derivedFrom":makeQuery(id+"F1.opExtrude","CAP_FACE",FACE,{"disambiguationData":[OSD([subQ6,subQ8,subQ9,subQ7,subQ4,subQ3,subQ2,subQ1,subQ0,subQ5,subQ10,subQ11])],"isStart":true})});}
            var sketch = newSketch(context, id + "F16", { "sketchPlane" : qUnion([Q0])});
            skCircle(sketch, "E79", {"center": v(0, 104.25) * mm, "radius": 6 * mm});
            skArc(sketch, "E80", {"start": v(15, 104.25) * mm, "mid": v(0, 119.25) * mm, "end": v(-15, 104.25) * mm});
            skLineSegment(sketch, "E81", {"start": v(-15, 104.25) * mm, "end": v(-15, 92.25) * mm});
            skLineSegment(sketch, "E82", {"start": v(15, 104.25) * mm, "end": v(15, 92.25) * mm});
            skLineSegment(sketch, "E83", {"start": v(-15, 92.25) * mm, "end": v(-33, 74.25) * mm});
            skLineSegment(sketch, "E84", {"start": v(15, 92.25) * mm, "end": v(33, 74.25) * mm});
            skPoint(sketch, "E85.start.orphan", {"position": v(0, 74.25) * mm});
            skLineSegment(sketch, "E86", {"start": v(0, 0) * mm, "end": v(74.25, 0) * mm});
            skLineSegment(sketch, "E87", {"start": v(0, 0) * mm, "end": v(-74.25, 0) * mm});
            skLineSegment(sketch, "E88.MirrorCS", {"start": v(15, -104.25) * mm, "end": v(15, -92.25) * mm});
            skLineSegment(sketch, "E89.MirrorCS", {"start": v(15, -92.25) * mm, "end": v(33, -74.25) * mm});
            skArc(sketch, "E90.MirrorCS", {"start": v(15, -104.25) * mm, "mid": v(0, -119.25) * mm, "end": v(-15, -104.25) * mm});
            skCircle(sketch, "E91.MirrorC", {"center": v(0, -104.25) * mm, "radius": 6 * mm});
            skLineSegment(sketch, "E92.MirrorCS", {"start": v(-15, -104.25) * mm, "end": v(-15, -92.25) * mm});
            skLineSegment(sketch, "E93.MirrorCS", {"start": v(-15, -92.25) * mm, "end": v(-33, -74.25) * mm});
            skSolve(sketch);
        }
        {
            var Q0;
            Q0=makeQuery(id+"F16.imprint","IMPRINT",FACE,{"disambiguationData":[TD([[makeQuery(id+"F16.imprint","IMPRINT",EDGE,{"derivedFrom":sQuery(id+"F16.wireOp",EDGE,"E88.MirrorCS")}),1.0]])]});
            var Q1;
            Q1=makeQuery(id+"F16.imprint","IMPRINT",FACE,{"disambiguationData":[TD([[makeQuery(id+"F16.imprint","IMPRINT",EDGE,{"derivedFrom":makeQuery(id+"F1.opExtrude","CAP_EDGE",EDGE,{"disambiguationData":[OSD([sQuery(id+"F0.wireOp",EDGE,"E6")])],"isStart":true})}),-1.0]])]});
            var Q2;
            Q2=makeQuery(id+"F16.imprint","IMPRINT",FACE,{"disambiguationData":[TD([[makeQuery(id+"F16.imprint","IMPRINT",EDGE,{"derivedFrom":makeQuery(id+"F1.opExtrude","CAP_EDGE",EDGE,{"disambiguationData":[OSD([sQuery(id+"F0.wireOp",EDGE,"E4")])],"isStart":true})}),-1.0]])]});
            var Q3;
            Q3=makeQuery(id+"F16.imprint","IMPRINT",FACE,{"disambiguationData":[TD([[makeQuery(id+"F16.imprint","IMPRINT",EDGE,{"derivedFrom":sQuery(id+"F16.wireOp",EDGE,"E79")}),-1.0]])]});
            extrude(context, id + "F17", {"entities" : qUnion([Q0, Q1, Q2, Q3]), "operationType" : NewBodyOperationType.ADD, "depth" : 3 * mm, "offsetDistance" : 25 * mm});
        }
    });
